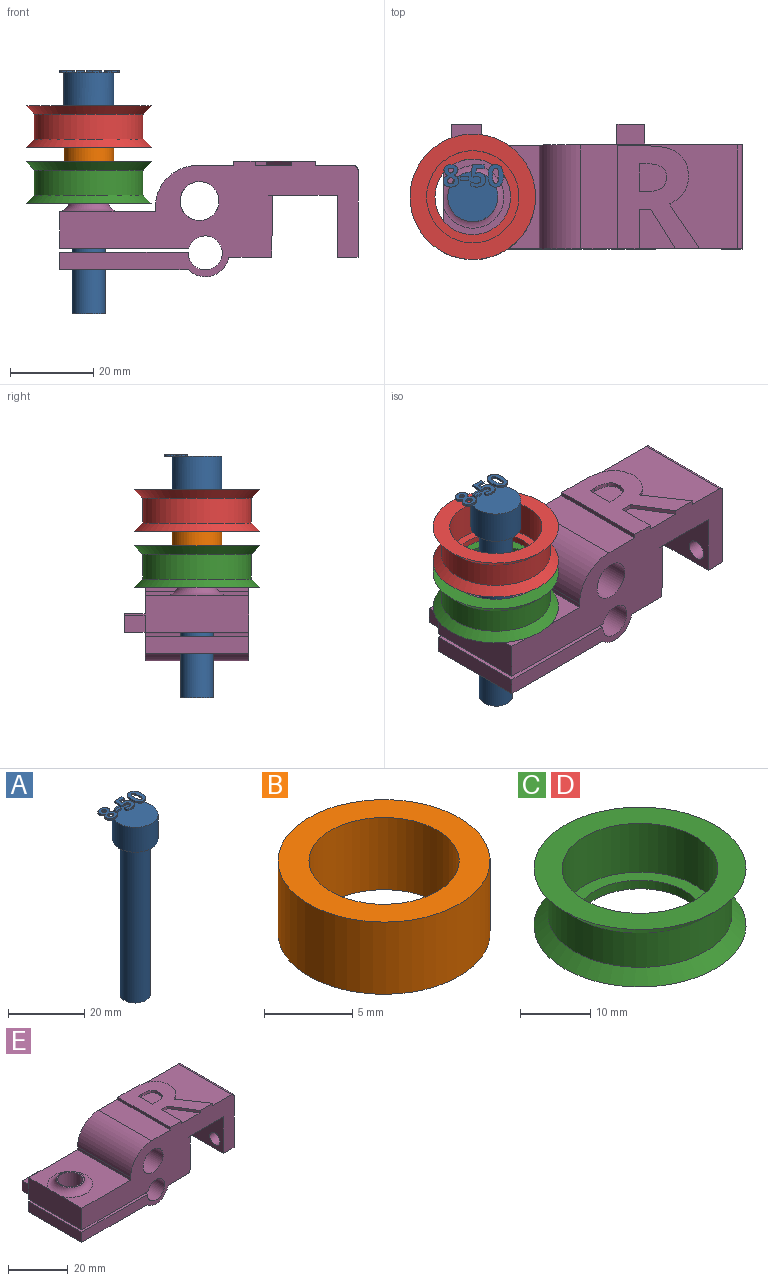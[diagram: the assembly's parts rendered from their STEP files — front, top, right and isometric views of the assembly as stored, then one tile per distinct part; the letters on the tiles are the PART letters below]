
ASSEMBLY  parts=5 mates=4
PART A: 86 faces, bbox 14.5x13.7x58.5 mm
  f0: plane 12x12mm, normal (0,0,1), area 99.4mm2, adj f5,f22,f23,f24,f25,f26,f40,f41
  f1: plane 1x0.26mm, normal (0,0,1), area 0.1mm2, adj f5,f46,f47,f48,f49
  f2: plane 0.85x0.68mm, normal (0,0,1), area 0.2mm2, adj f5,f29,f30,f31
  f3: cylinder r=4mm len=50mm, axis (0,0,-1), area 1256.6mm2, adj f4,f6
  f4: plane 8x8mm, normal (0,0,-1), area 50.3mm2, adj f3
  f5: cylinder r=6mm len=12mm, axis (0,0,-1), area 301.6mm2, adj f0,f1,f2,f6,f39,f45,f67,f85
  f6: plane 12x12mm, normal (0,0,-1), area 62.8mm2, adj f3,f5
  f7: extruded ~0.5x0.46mm, area 0.2mm2, adj f8,f37,f38,f39
  f8: extruded ~0.5x0.46mm, area 0.2mm2, adj f7,f9,f38,f39
  f9: extruded ~0.5x0.39mm, area 0.2mm2, adj f8,f10,f38,f39
  f10: extruded ~0.5x0.4mm, area 0.2mm2, adj f9,f11,f38,f39
  f11: extruded ~0.5x0.49mm, area 0.3mm2, adj f10,f12,f38,f39
  f12: extruded ~0.5x0.5mm, area 0.3mm2, adj f11,f13,f38,f39
  f13: extruded ~0.5x0.39mm, area 0.2mm2, adj f12,f37,f38,f39
  f14: extruded ~1.22x0.5mm, area 0.6mm2, adj f15,f35,f38,f39
  f15: extruded ~1.22x0.5mm, area 0.6mm2, adj f14,f16,f38,f39
  f16: extruded ~0.91x0.5mm, area 0.5mm2, adj f15,f17,f38,f39
  f17: extruded ~0.71x0.5mm, area 0.4mm2, adj f16,f18,f38,f39
  f18: extruded ~0.65x0.61mm, area 0.4mm2, adj f17,f19,f38,f39
  f19: extruded ~0.77x0.62mm, area 0.5mm2, adj f18,f20,f38,f39
  f20: extruded ~0.8x0.5mm, area 0.4mm2, adj f19,f21,f38,f39
  f21: extruded ~1.04x0.5mm, area 0.6mm2, adj f20,f22,f38,f39
  f22: extruded ~1.36x0.5mm, area 0.7mm2, adj f0,f21,f23,f38,f39
  f23: extruded ~1.33x0.5mm, area 0.7mm2, adj f0,f22,f24,f38
  f24: extruded ~1.04x0.51mm, area 0.6mm2, adj f0,f23,f25,f38
  f25: extruded ~0.75x0.5mm, area 0.4mm2, adj f0,f24,f26,f38
  f26: extruded ~0.85x0.66mm, area 0.5mm2, adj f0,f25,f27,f38,f39
  f27: extruded ~0.72x0.56mm, area 0.5mm2, adj f26,f28,f38,f39
  f28: extruded ~0.72x0.5mm, area 0.4mm2, adj f27,f35,f38,f39
  f29: extruded ~0.5x0.45mm, area 0.3mm2, adj f2,f30,f36,f38,f39
  f30: extruded ~0.5x0.47mm, area 0.3mm2, adj f2,f29,f31,f38
  f31: extruded ~0.62x0.5mm, area 0.3mm2, adj f2,f30,f32,f38,f39
  f32: extruded ~0.59x0.5mm, area 0.3mm2, adj f31,f33,f38,f39
  f33: extruded ~0.5x0.48mm, area 0.3mm2, adj f32,f34,f38,f39
  f34: extruded ~0.89x0.77mm, area 0.6mm2, adj f33,f36,f38,f39
  f35: extruded ~0.93x0.5mm, area 0.5mm2, adj f14,f28,f38,f39
  f36: extruded ~0.66x0.5mm, area 0.4mm2, adj f29,f34,f38,f39
  f37: extruded ~0.5x0.39mm, area 0.2mm2, adj f7,f13,f38,f39
  f38: plane 5.4x3.69mm, normal (0,0,1), area 12.7mm2, adj f7,f8,f9,f10,f11,f12,f13,f14
  f39: plane 5.4x3.53mm, normal (0,0,-1), area 10.2mm2, adj f5,f7,f8,f9,f10,f11,f12,f13
  f40: plane 0.9x0.5mm, normal (-1,0,0), area 0.4mm2, adj f0,f41,f43,f44
  f41: plane 1.93x0.5mm, normal (0,-1,0), area 1mm2, adj f0,f40,f42,f44
  f42: plane 0.9x0.5mm, normal (1,0,0), area 0.4mm2, adj f0,f41,f43,f44
  f43: plane 1.93x0.5mm, normal (0,1,0), area 1mm2, adj f0,f40,f42,f44
  f44: plane 1.93x0.9mm, normal (0,0,1), area 1.7mm2, adj f40,f41,f42,f43
  f45: plane 0.76x0.31mm, normal (0,0,-1), area 0mm2, adj f5,f46
  f46: extruded ~1.21x0.5mm, area 0.7mm2, adj f0,f1,f45,f47,f65,f66
  f47: extruded ~0.54x0.5mm, area 0.3mm2, adj f1,f46,f48,f66
  f48: plane 0.5x0.13mm, normal (-0.2,0.98,0), area 0.1mm2, adj f1,f47,f49,f66
  f49: plane 1.03x0.5mm, normal (1,-0.09,0), area 0.5mm2, adj f1,f48,f50,f66,f67
  f50: plane 1.88x0.5mm, normal (0,-1,0), area 0.9mm2, adj f49,f51,f66,f67
  f51: plane 0.94x0.5mm, normal (1,0,0), area 0.5mm2, adj f50,f52,f66,f67
  f52: plane 2.85x0.5mm, normal (0,1,0), area 1.4mm2, adj f51,f53,f66,f67
  f53: plane 2.68x0.5mm, normal (-1,0.07,0), area 1.3mm2, adj f0,f52,f54,f66,f67
  f54: plane 0.5x0.44mm, normal (-0.47,-0.88,0), area 0.3mm2, adj f0,f53,f55,f66
  f55: extruded ~0.5x0.37mm, area 0.2mm2, adj f0,f54,f56,f66
  f56: extruded ~0.5x0.42mm, area 0.2mm2, adj f0,f55,f57,f66
  f57: extruded ~1.05x0.8mm, area 0.8mm2, adj f0,f56,f58,f66
  f58: extruded ~1.02x0.83mm, area 0.8mm2, adj f0,f57,f59,f66
  f59: extruded ~0.72x0.5mm, area 0.4mm2, adj f0,f58,f60,f66
  f60: extruded ~0.66x0.5mm, area 0.4mm2, adj f0,f59,f61,f66
  f61: plane 0.96x0.5mm, normal (-1,0,0), area 0.5mm2, adj f0,f60,f62,f66
  f62: extruded ~1.42x0.5mm, area 0.7mm2, adj f0,f61,f63,f66
  f63: extruded ~1.55x0.5mm, area 0.8mm2, adj f0,f62,f64,f66
  f64: extruded ~1.36x0.54mm, area 0.8mm2, adj f0,f63,f65,f66
  f65: extruded ~1.17x0.5mm, area 0.6mm2, adj f0,f46,f64,f66
  f66: plane 5.33x3.51mm, normal (0,0,1), area 10.9mm2, adj f46,f47,f48,f49,f50,f51,f52,f53
  f67: plane 2.97x1.71mm, normal (0,0,-1), area 3.5mm2, adj f5,f49,f50,f51,f52,f53
  f68: extruded ~1.39x0.5mm, area 0.7mm2, adj f69,f83,f84,f85
  f69: extruded ~1.39x0.5mm, area 0.7mm2, adj f68,f70,f84,f85
  f70: extruded ~0.56x0.5mm, area 0.4mm2, adj f69,f71,f84,f85
  f71: extruded ~0.56x0.5mm, area 0.4mm2, adj f70,f72,f84,f85
  f72: extruded ~1.39x0.5mm, area 0.7mm2, adj f71,f73,f84,f85
  f73: extruded ~1.38x0.5mm, area 0.7mm2, adj f72,f74,f84,f85
  f74: extruded ~0.56x0.5mm, area 0.4mm2, adj f73,f83,f84,f85
  f75: extruded ~2.04x0.5mm, area 1.1mm2, adj f76,f82,f84,f85
  f76: extruded ~2.02x0.5mm, area 1.1mm2, adj f75,f77,f84,f85
  f77: extruded ~1.38x0.69mm, area 0.8mm2, adj f76,f78,f84,f85
  f78: extruded ~1.38x0.66mm, area 0.8mm2, adj f77,f79,f84,f85
  f79: extruded ~2.05x0.5mm, area 1.1mm2, adj f78,f80,f84,f85
  f80: extruded ~2.02x0.5mm, area 1mm2, adj f0,f79,f81,f84,f85
  f81: extruded ~1.37x0.68mm, area 0.8mm2, adj f0,f80,f82,f84
  f82: extruded ~1.39x0.66mm, area 0.8mm2, adj f0,f75,f81,f84,f85
  f83: extruded ~0.56x0.5mm, area 0.4mm2, adj f68,f74,f84,f85
  f84: plane 5.41x3.68mm, normal (0,0,1), area 12.1mm2, adj f68,f69,f70,f71,f72,f73,f74,f75
  f85: plane 5.41x3.68mm, normal (0,0,-1), area 10.3mm2, adj f5,f68,f69,f70,f71,f72,f73,f74
PART B: 4 faces, bbox 12x12x5 mm
  f0: cylinder r=4.25mm len=8.5mm, axis (0,0,-1), area 133.5mm2, adj f2,f3
  f1: cylinder r=6mm len=12mm, axis (0,0,-1), area 188.5mm2, adj f2,f3
  f2: plane 12x12mm, normal (0,0,1), area 56.4mm2, adj f0,f1
  f3: plane 12x12mm, normal (0,0,-1), area 56.4mm2, adj f0,f1
PART C: 8 faces, bbox 30.2x30.2x10 mm
  f0: plane 30.2x30.2mm, normal (0,0,1), area 329.2mm2, adj f1,f7
  f1: cylinder r=11.1mm len=22.2mm, axis (0,0,-1), area 592.8mm2, adj f0,f2
  f2: plane 22.2x22.2mm, normal (0,0,1), area 126.9mm2, adj f1,f3
  f3: cylinder r=9.1mm len=18.2mm, axis (0,0,-1), area 85.8mm2, adj f2,f4
  f4: plane 30.2x30.2mm, normal (0,0,-1), area 456.2mm2, adj f3,f5
  f5: cone r=13.1mm half-angle=45deg, axis (0,0,-1), area 250.6mm2, adj f4,f6
  f6: cylinder r=13.1mm len=26.2mm, axis (0,0,-1), area 493.9mm2, adj f5,f7
  f7: cone r=15.1mm half-angle=45deg, axis (0,0,1), area 250.6mm2, adj f0,f6
PART D: same geometry as C
PART E: 58 faces, bbox 75.2x30x27.7 mm
  f0: plane 37.77x25mm, normal (0,0,1), area 550.8mm2, adj f13,f14,f24,f26,f39,f40,f41,f42
  f1: plane 9.51x8.71mm, normal (0,0,1), area 54.7mm2, adj f13,f36,f37,f38
  f2: plane 25x4.12mm, normal (-1,0,0), area 103mm2, adj f5,f13,f14,f18
  f3: cylinder r=4.17mm len=8.35mm, axis (0,0,1), area 108.1mm2, adj f5,f18
  f4: plane 25x9.34mm, normal (0,0,-1), area 233.4mm2, adj f13,f14,f16,f56
  f5: plane 30.88x25mm, normal (0,0,-1), area 717.2mm2, adj f2,f3,f13,f14,f16
  f6: plane 25x8.82mm, normal (-1,0,0), area 219.6mm2, adj f7,f13,f14,f19,f23
  f7: plane 25x23mm, normal (0,0,1), area 400mm2, adj f6,f8,f13,f14,f23
  f8: plane 25x1.1mm, normal (-1,0,0), area 27.5mm2, adj f7,f13,f14,f24
  f9: plane 25x21.09mm, normal (1,0,0), area 493.5mm2, adj f10,f13,f14,f21,f22,f26
  f10: plane 25x5mm, normal (0,0,-1), area 125mm2, adj f9,f11,f13,f14
  f11: plane 25x15mm, normal (-1,0,0), area 341.3mm2, adj f10,f12,f13,f14,f21,f22
  f12: plane 25x16.55mm, normal (0,0,-1), area 413.8mm2, adj f11,f13,f14,f55
  f13: plane 71.77x27.75mm, normal (0,-1,0), area 1057.8mm2, adj f0,f1,f2,f4,f5,f6,f7,f8
  f14: plane 71.77x26.75mm, normal (0,1,0), area 986.7mm2, adj f0,f2,f4,f5,f6,f7,f8,f9
  f15: cylinder r=4.17mm len=10.78mm, axis (0,0,1), area 282.8mm2, adj f19,f20
  f16: cylinder r=5.75mm len=25mm, axis (0,-1,0), area 315.9mm2, adj f4,f5,f13,f14
  f17: cylinder r=4.1mm len=25mm, axis (0,-1,0), area 618.7mm2, adj f13,f14,f18,f19
  f18: plane 30.91x25mm, normal (0,0,1), area 718.1mm2, adj f2,f3,f13,f14,f17
  f19: plane 31.07x30mm, normal (0,0,-1), area 758.4mm2, adj f6,f13,f14,f15,f17,f28,f29,f30
  f20: plane 9.35x9.35mm, normal (0,0,1), area 13.9mm2, adj f15,f23
  f21: cylinder r=2.43mm len=5mm, axis (1,0,0), area 76.2mm2, adj f9,f11
  f22: cylinder r=2.2mm len=5mm, axis (1,0,0), area 69.1mm2, adj f9,f11
  f23: torus R=7.5mm, axis (0,0,-1), area 134.6mm2, adj f6,f7,f20
  f24: cylinder r=10mm len=25mm, axis (0,-1,0), area 392.7mm2, adj f0,f8,f13,f14
  f25: cylinder r=4.68mm len=25mm, axis (0,-1,0), area 735.2mm2, adj f13,f14
  f26: cylinder r=1mm len=25mm, axis (0,-1,0), area 39.3mm2, adj f0,f9,f13,f14
  f27: plane 7.3x5mm, normal (0,0,1), area 36.5mm2, adj f14,f28,f29,f30
  f28: plane 5x4.12mm, normal (-1,0,0), area 20.6mm2, adj f14,f19,f27,f30
  f29: plane 5x4.12mm, normal (1,0,0), area 20.6mm2, adj f14,f19,f27,f30
  f30: plane 7.3x4.12mm, normal (0,1,0), area 30.1mm2, adj f19,f27,f28,f29
  f31: plane 6.63x5mm, normal (0,0,1), area 33.2mm2, adj f14,f32,f34,f35
  f32: plane 5x4.5mm, normal (-1,0,0), area 22.5mm2, adj f14,f31,f33,f35
  f33: plane 6.63x5mm, normal (0,0,-1), area 33.2mm2, adj f14,f32,f34,f35
  f34: plane 5x4.5mm, normal (1,0,0), area 22.5mm2, adj f14,f31,f33,f35
  f35: plane 6.63x4.5mm, normal (0,1,0), area 29.9mm2, adj f31,f32,f33,f34
  f36: plane 9.51x1mm, normal (1,0,0), area 9.5mm2, adj f1,f13,f37,f53
  f37: plane 2.79x1mm, normal (0,-1,0), area 2.8mm2, adj f1,f36,f38,f53
  f38: plane 9.51x5.92mm, normal (-0.85,-0.53,0), area 11.2mm2, adj f1,f13,f37,f53
  f39: extruded ~10.8x7.29mm, area 13mm2, adj f0,f13,f40,f53
  f40: extruded ~3.41x2.67mm, area 4.4mm2, adj f0,f39,f41,f53
  f41: extruded ~3.89x1.2mm, area 4.1mm2, adj f0,f40,f42,f53
  f42: extruded ~5.59x2.42mm, area 6.3mm2, adj f0,f41,f43,f53
  f43: extruded ~7.48x1.84mm, area 7.8mm2, adj f0,f42,f44,f53
  f44: plane 7.22x1mm, normal (0,1,0), area 7.2mm2, adj f0,f43,f45,f53
  f45: plane 24.79x1mm, normal (-1,0,0), area 24.8mm2, adj f0,f13,f44,f53
  f46: plane 1.69x1mm, normal (0,1,0), area 1.7mm2, adj f47,f52,f53,f54
  f47: plane 6.7x1mm, normal (1,0,0), area 6.7mm2, adj f46,f48,f53,f54
  f48: plane 1.6x1mm, normal (0,-1,0), area 1.6mm2, adj f47,f49,f53,f54
  f49: extruded ~3.75x1mm, area 3.9mm2, adj f48,f50,f53,f54
  f50: extruded ~2.51x1.21mm, area 2.9mm2, adj f49,f51,f53,f54
  f51: extruded ~2.61x1.19mm, area 3mm2, adj f50,f52,f53,f54
  f52: extruded ~3.68x1mm, area 3.8mm2, adj f46,f51,f53,f54
  f53: plane 24.79x19.8mm, normal (0,0,1), area 300mm2, adj f13,f36,f37,f38,f39,f40,f41,f42
  f54: plane 6.7x6.56mm, normal (0,0,1), area 38.8mm2, adj f46,f47,f48,f49,f50,f51,f52
  f55: plane 25x1mm, normal (0.01,0,1), area 25mm2, adj f12,f13,f14,f57
  f56: plane 25x1mm, normal (-0.01,0,-1), area 25mm2, adj f4,f13,f14,f57
  f57: plane 25x14.91mm, normal (1,0,-0.01), area 372.8mm2, adj f13,f14,f55,f56
PLACE A t=(-103.78,-12.5,-13.6)mm
PLACE B rot(axis=(1,0,0),180deg) t=(-103.78,-12.5,26.4)mm
PLACE C t=(-103.78,-12.5,18.1)mm
PLACE D t=(-103.78,-12.5,31.6)mm
PLACE E at identity
MATE fastened A.f3 <-> D.f1  axis (0,0,-1) through (-103.78,-12.5,36.4)mm
MATE fastened B.f0 <-> C.f1  axis (0,0,1) through (-103.78,-12.5,21.4)mm
MATE fastened C.f1 <-> E.f3  axis (0,0,-1) through (-103.78,-12.5,12.9)mm
MATE fastened D.f1 <-> B.f0  axis (0,0,-1) through (-103.78,-12.5,26.4)mm
